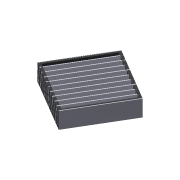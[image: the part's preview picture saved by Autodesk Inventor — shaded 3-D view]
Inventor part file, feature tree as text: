
AUTODESK INVENTOR PART (.ipt)
format: ipt  version: 2016 (Build 200138000, 138)  size: 191,488 bytes
history: native  units: mm
features: extrude x3, sketch x3, projected_geometry x3, pattern_linear x1, reference x1
ambient origin geometry x8: Origin, YZ Plane, XZ Plane, XY Plane, X Axis, Y Axis, Z Axis, Center Point
bodies: Solid1 (feature_tree), Solid2 (feature_tree)
feature tree (11):
  extrude  "Extrusion1"  Depth=20.0mm
  extrude  "Extrusion2"  Depth=2.0mm
  pattern_linear  "Rectangular Pattern1"  Spacing1=1.0mm  [1 undecoded]
  extrude  "Extrusion3"  Depth=20.0mm
  sketch  "Sketch1"  dims[d0=20.0mm d1=0.0mm d2=3.490659mm]
  reference  "Reference1"
  sketch  "Sketch2"  dims[d3=1.745329mm d4=2.0mm]
  projected_geometry  "Projected Loop1"
  sketch  "Sketch3"  dims[d5=3.490659mm d6=1.0mm d7=2.0mm d8=1.0mm d9=100.0mm d10=0.0mm d11=100.0mm d13=7.5mm d14=3.0mm d15=20.0mm d16=0.0mm]
  projected_geometry  "Projected Loop2"
  projected_geometry  "Projected Loop3"
note: 1 required parameter value undecoded (feature->parameter linkage not recoverable at this tier; creation-order binding heuristic only, values carry confidence <= 0.55)
